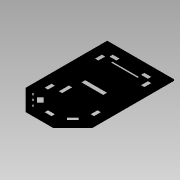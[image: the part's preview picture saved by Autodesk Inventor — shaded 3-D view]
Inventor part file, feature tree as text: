
AUTODESK INVENTOR PART (.ipt)
format: ipt  version: 2015 SP1 (Build 190203100, 203)  size: 347,648 bytes
history: native  units: mm
features: extrude x1, sketch x1
ambient origin geometry x8: Origin, YZ Plane, XZ Plane, XY Plane, X Axis, Y Axis, Z Axis, Center Point
bodies: Body1 (feature_tree)
feature tree (2):
  extrude  "Extrusion2"  Depth=30.0mm
  sketch  "Sketch1"  dims[d104=30.0mm d106=23.0mm d107=30.0mm d109=23.0mm d113=30.0mm d115=32.5mm d116=30.0mm d118=32.5mm d121=172.234468mm d122=140.811657mm d123=172.234468mm d124=58.326098mm d125=58.326098mm d126=58.326098mm d127=23.561995mm d128=23.561874mm d129=23.562018mm d130=23.561892mm d131=15.707985mm d132=15.707942mm d134=10.0mm d135=9.999879mm d136=10.0mm d137=10.0mm d138=10.0mm d141=3.0mm d142=0.0mm d145=80.297969mm]
